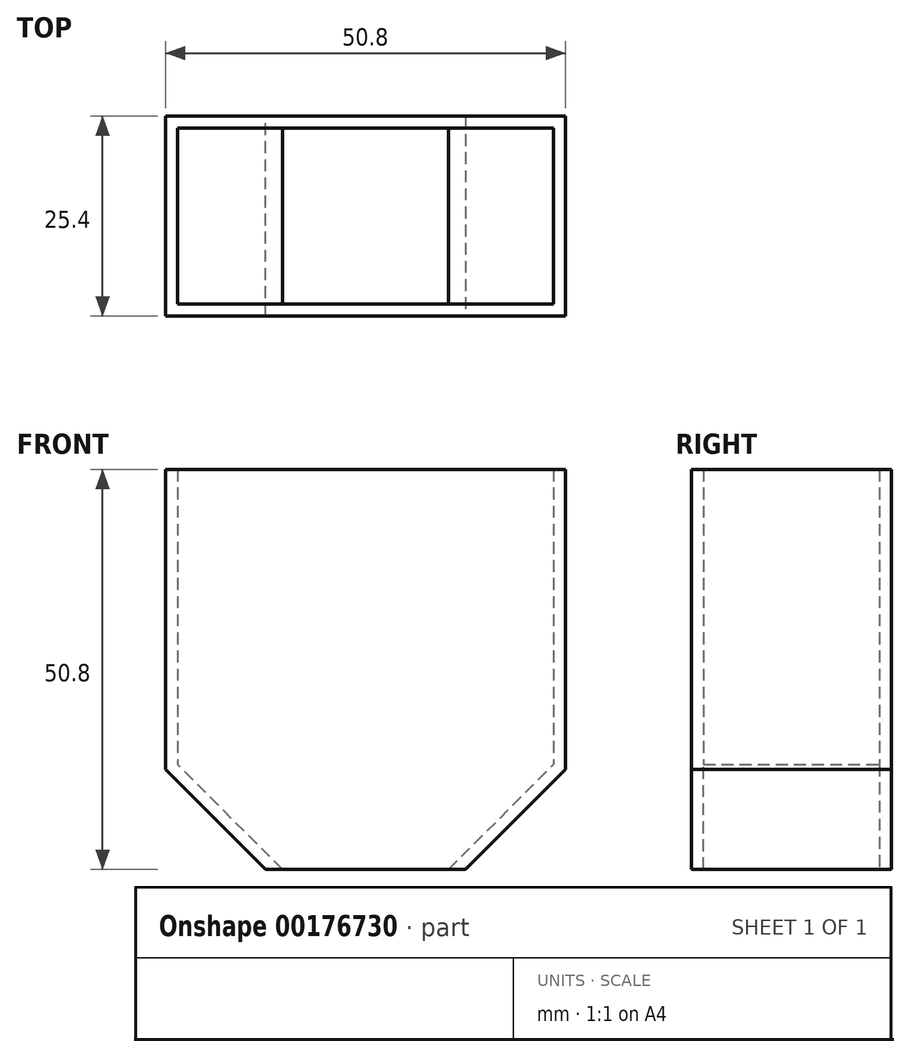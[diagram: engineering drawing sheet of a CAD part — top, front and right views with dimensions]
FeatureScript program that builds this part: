
annotation { "Feature Type Name" : "Feature", "Feature Type Description" : "" }
export const myFeature = defineFeature(function(context is Context, id is Id, definition is map)
    precondition{}
    {
        {
            var Q0;
            Q0=qCreatedBy(makeId("Front.planeOp"),FACE);
            var sketch = newSketch(context, id + "F0", { "sketchPlane" : qUnion([Q0])});
            skLineSegment(sketch, "E0.bottom", {"start": v(-25.4, 50.8) * mm, "end": v(25.4, 50.8) * mm});
            skLineSegment(sketch, "E0.top", {"start": v(-25.4, 0) * mm, "end": v(25.4, 0) * mm});
            skLineSegment(sketch, "E0.left", {"start": v(-25.4, 50.8) * mm, "end": v(-25.4, 0) * mm});
            skLineSegment(sketch, "E0.right", {"start": v(25.4, 50.8) * mm, "end": v(25.4, 0) * mm});
            skSolve(sketch);
        }
        {
            var Q0;
            Q0 = qSketchRegion(id + "F0", true);
            extrude(context, id + "F1", {"entities" : qUnion([Q0]), "endBound" : BoundingType.SYMMETRIC, "depth" : 25.4 * mm});
        }
        {
            var Q0;
            Q0=makeQuery(id+"F1.opExtrude","SWEPT_EDGE",EDGE,{"disambiguationData":[OSD([sQuery(id+"F0.wireOp",EDGE,"E0.top"),sQuery(id+"F0.wireOp",EDGE,"E0.left")])]});
            var Q1;
            Q1=makeQuery(id+"F1.opExtrude","SWEPT_EDGE",EDGE,{"disambiguationData":[OSD([sQuery(id+"F0.wireOp",EDGE,"E0.top"),sQuery(id+"F0.wireOp",EDGE,"E0.right")])]});
            chamfer(context, id + "F2", {"entities" : qUnion([Q0, Q1]), "width" : 12.7 * mm, "tangentPropagation" : true});
        }
        {
            var Q0;
            Q0=makeQuery(id+"F1.opExtrude","SWEPT_FACE",FACE,{"disambiguationData":[OSD([sQuery(id+"F0.wireOp",EDGE,"E0.bottom")])]});
            var Q1;
            Q1=makeQuery(id+"F1.opExtrude","SWEPT_FACE",FACE,{"disambiguationData":[OSD([sQuery(id+"F0.wireOp",EDGE,"E0.top")])]});
            shell(context, id + "F3", {"entities" : qUnion([Q0, Q1]), "thickness" : 1.52 * mm});
        }
    });
